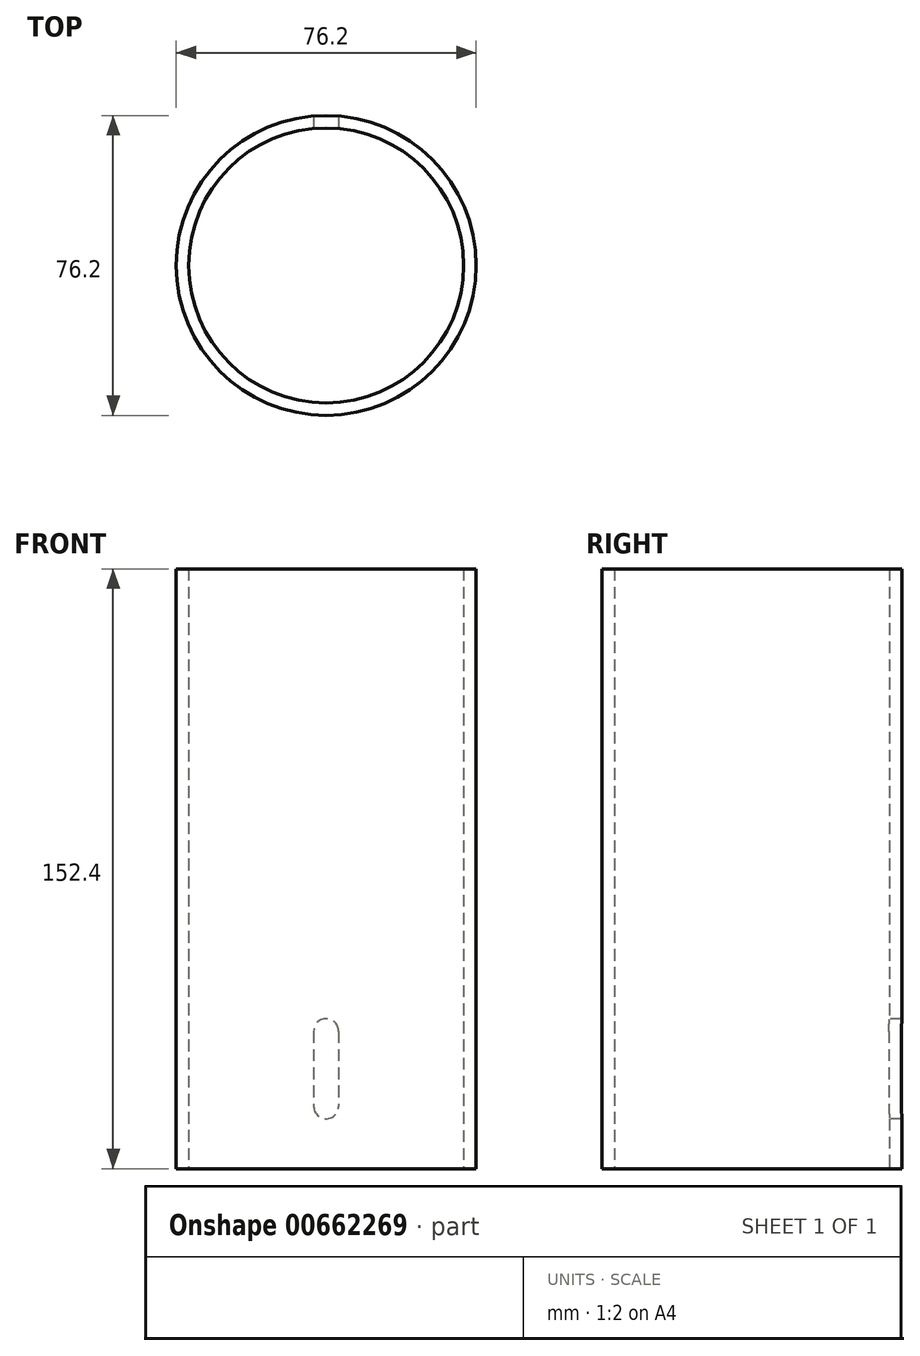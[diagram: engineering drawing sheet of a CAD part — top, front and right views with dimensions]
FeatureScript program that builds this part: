
annotation { "Feature Type Name" : "Feature", "Feature Type Description" : "" }
export const myFeature = defineFeature(function(context is Context, id is Id, definition is map)
    precondition{}
    {
        {
            var Q0;
            Q0=qCreatedBy(makeId("Top.planeOp"),FACE);
            var sketch = newSketch(context, id + "F0", { "sketchPlane" : qUnion([Q0])});
            skCircle(sketch, "E0", {"center": v(0, 0) * mm, "radius": 38.1 * mm});
            skCircle(sketch, "E1", {"center": v(0, 0) * mm, "radius": 34.93 * mm});
            skSolve(sketch);
        }
        {
            var Q0;
            Q0=qSketchRegion(id+"F0",true);
            extrude(context, id + "F1", {"entities" : qUnion([Q0]), "depth" : 152.4 * mm});
        }
        {
            var Q0;
            Q0=qCreatedBy(makeId("Front.planeOp"),FACE);
            var sketch = newSketch(context, id + "F2", { "sketchPlane" : qUnion([Q0])});
            skLineSegment(sketch, "E2.left", {"start": v(3.17, 15.87) * mm, "end": v(3.17, 34.93) * mm});
            skLineSegment(sketch, "E2.right", {"start": v(-3.18, 15.87) * mm, "end": v(-3.18, 34.93) * mm});
            skPoint(sketch, "E2.middle", {"position": v(0, 25.4) * mm});
            skArc(sketch, "E3", {"start": v(3.17, 34.93) * mm, "mid": v(0, 38.1) * mm, "end": v(-3.17, 34.93) * mm});
            skArc(sketch, "E4", {"start": v(-3.17, 15.87) * mm, "mid": v(0, 12.7) * mm, "end": v(3.17, 15.87) * mm});
            skLineSegment(sketch, "E5", {"start": v(0, 34.93) * mm, "end": v(0, 15.87) * mm});
            skSolve(sketch);
        }
        {
            var Q0;
            Q0=makeQuery(id+"F2.imprint","IMPRINT",FACE,{"disambiguationData":[TD([[makeQuery(id+"F2.imprint","IMPRINT",EDGE,{"derivedFrom":sQuery(id+"F2.wireOp",EDGE,"E2.left")}),1.0]])]});
            extrude(context, id + "F3", {"entities" : qUnion([Q0]), "operationType" : NewBodyOperationType.REMOVE, "endBound" : BoundingType.THROUGH_ALL, "oppositeDirection" : true, "depth" : 25.4 * mm, "offsetDistance" : 25.4 * mm});
        }
    });
